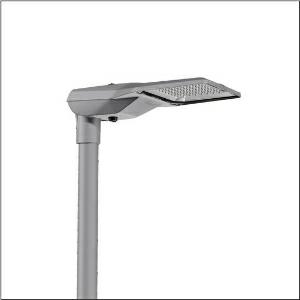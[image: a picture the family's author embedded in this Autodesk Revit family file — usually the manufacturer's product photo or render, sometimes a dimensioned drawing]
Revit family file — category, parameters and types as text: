
# Revit family: streetlight_sl_21_midi___stw1_0a_5xe3e33t08nb_95e0
name_source: partatom
category: Lighting Fixtures
units: mm (PartAtom-declared; Revit-internal decimal feet)

## family parameters
Cut with Voids When Loaded = No
Host = Face
Light Source = No
Part Type = Normal
Room Calculation Point = No
Round Connector Dimension = Use Diameter
Shared = No

## types (1)
- --- (1 x LED, 22700 lm, 151.2 W, 3000K)
    Apparent Load = 151 VA
    CIE Flux Codes = 39 75 98 100 100
    Color Rendering = 70
    Color Temperature = 3000K
    Default Elevation = 1800 mm
    Description = Streetlight SL 21 midi, mast luminaire, primary light control with lens, of PMMA, primary optical cover: cover, of toughened safety glass, transparent, light distribution: STW1.0a, light emission: direct distribution, primary light characteristic: asymmetric, installation type: side-entry, post-top, LED, High Power LED, rated luminous flux: 22.700lm, luminous efficacy: 150lm/W, light colour: 730, colour temperature: 3000K, control gear: D4i, control: overheat protection, constant luminous flux control, time-dependent luminous flux control, flexible luminous flux parameterisation, pre-setting: logarithmic dimming characteristic, mains connection: 230..240V, AC, 50/60Hz, start of lifetime: 151W, end of service life: 157W, reduction: 70W, luminaire housing, of diecast aluminium, powder-coated, Siteco® metallic grey (DB 702S), corrosivity category C5 mid according to DIN EN ISO 12944, please order mast flange separately, inclination adjustable: 0°, 5°, 10°, 15°, sealing non-destructively replaceable, multi-level sealing system, length: 644mm, width: 335mm, height: 110mm, mast flange for spigot size: 42mm (side-entry): 5XC10008XM4, 60/48mm (side-entry/post-top): 5XC10108XM2, 76/60mm (side-entry/post-top): 5XC10108XM1, mounting height: 4..8m, Smart Interface below and above, protection rating (complete): IP66, insulation class (complete): insulation class II (safety insulation), certification: CE, ENEC, ENEC+, VDE, impact resistance: IK10, permissible operating ambient temperature for outdoor applications: -40..+50°C, standard-compliant lighting for roads and squares, packaging unit: 1 piece

Light Distribution: STW1.0a
    Height = 111 mm
    Lamp = 1 x LED
    Lamp Light Flux = 22700 lm
    Lamp Power = 151.2 W
    Lamp count = 1
    Length = 644 mm
    Luminous efficacy = 150 lm/W
    Manufacturer = Siteco
    ModVariant = No
    Model = 5XE3E33T08NB
    Number of Poles = 1
    OnlyDefault = Yes
    Power Factor = 1
    Product Name = Streetlight SL 21 midi | STW1.0a
    Product group = mast luminaire | pylon top
    ProductGroupID = 6100
    Protection Class = Protection class II
    Protection Degree = IP 66
    RLX_Detail_Level = 1
    RLX_Emergency_Light_Flux = 0 lm
    RLX_Emergency_Type = 0
    RLX_Emergency_Type_DB = No
    RlxData = <blob elided: 27141 chars, md5=e504ee7a>
    Socket = socket
    Standby Power = 0 W
    System Light Flux = 22700 lm
    System Power = 151 W
    Type Comments = factory setting: luminous flux: 100 % | dim-lin: 254 | 802 mA
    Type Image = l_1004304.jpg
    URL = http://relux.com
    VarID = @adj_191037
    Voltage = 0 V
    Weight = 0.00 kg
    Width = 336 mm

## geometry (parser evidence)
native form markers: Blend x4, Sweep x13
no freeform markers — native parametric forms only
